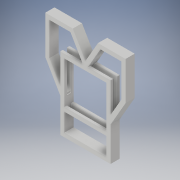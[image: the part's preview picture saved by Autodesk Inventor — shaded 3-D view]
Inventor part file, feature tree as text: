
AUTODESK INVENTOR PART (.ipt)
format: ipt  version: 2017 (Build 210142000, 142)  size: 271,872 bytes
history: native  units: in
note: dims shown in document units (in); Inventor stores cm internally (conversion verified against a paired STEP export)
features: extrude x5, sketch x5, other x2
ambient origin geometry x8: Origin, YZ Plane, XZ Plane, XY Plane, X Axis, Y Axis, Z Axis, Center Point
bodies: Body1 (feature_tree)
feature tree (12):
  other  "rame of door"
  extrude  "frame"  Depth=100.0in
  other  "middle of part"
  extrude  "door slot bottom"  Depth=10.0in
  extrude  "top left and right slots"  Depth=10.0in
  extrude  "slots for hiding bars"  Depth=22.0in
  extrude  "door recieves"  Depth=10.0in TaperAngle=0.0deg
  sketch  "Sketch1"  dims[d0=100.0in d1=100.0in]
  sketch  "Sketch7"  dims[d3=10.0in d4=10.0in]
  sketch  "Sketch8"  dims[d5=10.0in d6=10.0in]
  sketch  "Sketch12"  dims[d7=22.0in d8=0.0in d118=0.7071in d178=0.8316in]
  sketch  "Sketch13"  dims[d459=10.0in d460=0.0in d865=10.0in d866=0.0in d878=60.0deg d889=2.0in d890=1.0in d891=1.0in d893=1.0in d894=1.0in d895=1.0in d898=20.0in d899=0.0in d901=2.0in d902=78.8675in d903=51.0in d907=10.0in d916=10.0in d917=10.0in d919=10.0in d920=10.0in d921=10.0in d922=22.0in d923=0.0in d926=25.7957in d927=52.0in]
